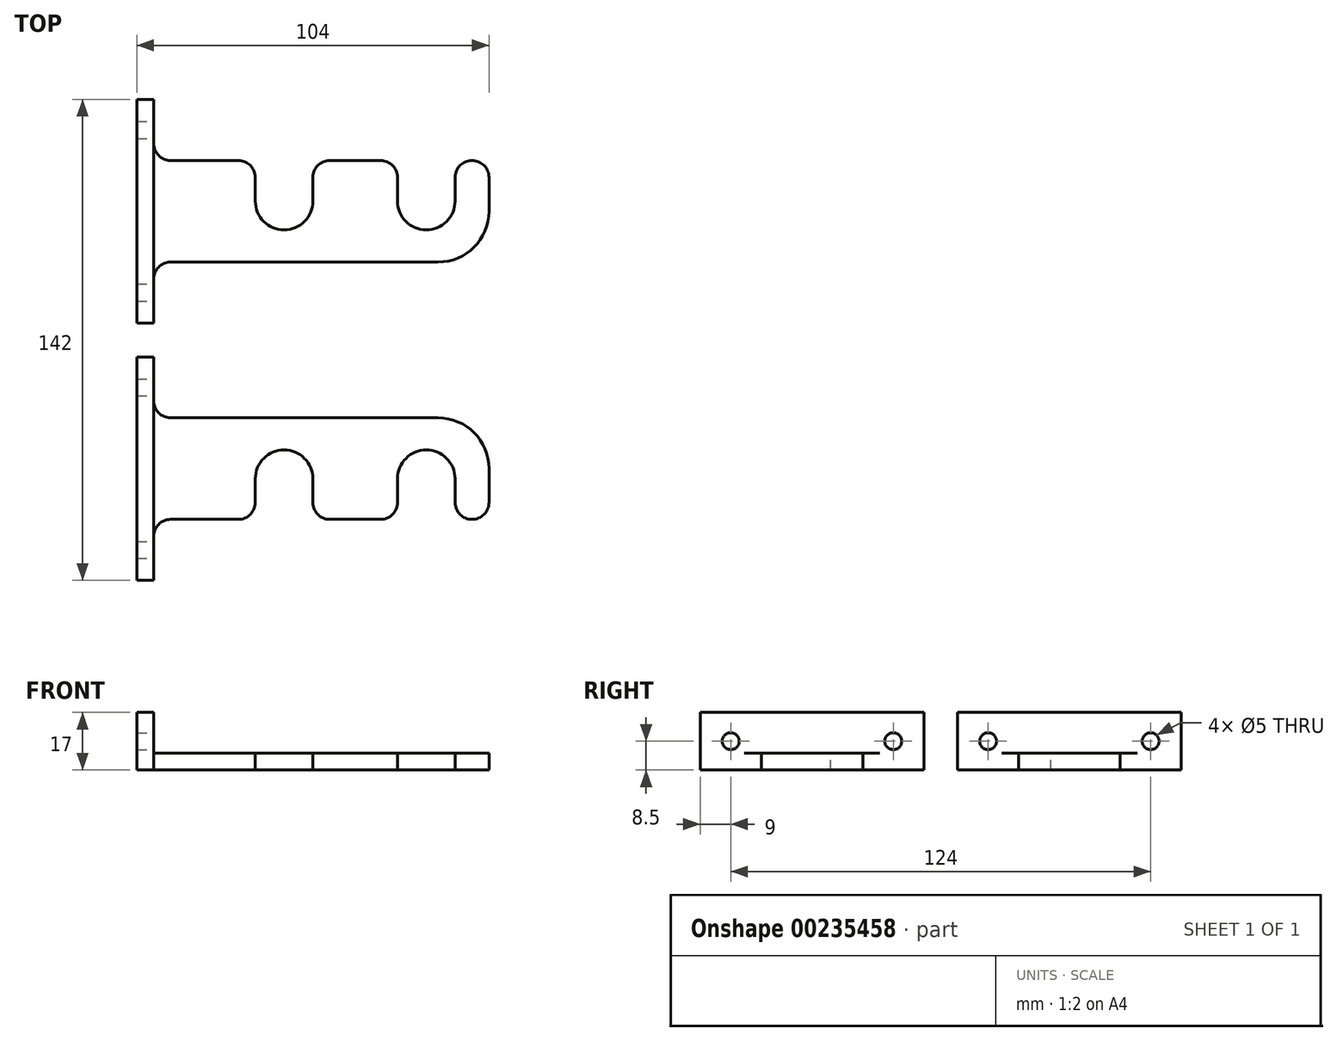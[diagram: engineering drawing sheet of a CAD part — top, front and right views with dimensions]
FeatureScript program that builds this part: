
annotation { "Feature Type Name" : "Feature", "Feature Type Description" : "" }
export const myFeature = defineFeature(function(context is Context, id is Id, definition is map)
    precondition{}
    {
        {
            var Q0;
            Q0=qCreatedBy(makeId("Front.planeOp"),FACE);
            var sketch = newSketch(context, id + "F0", { "sketchPlane" : qUnion([Q0])});
            skArc(sketch, "E0", {"start": v(28.28, 12.5) * mm, "mid": v(36.78, 4) * mm, "end": v(45.28, 12.5) * mm});
            skArc(sketch, "E1", {"start": v(70.28, 12.5) * mm, "mid": v(78.78, 4) * mm, "end": v(87.28, 12.5) * mm});
            skLineSegment(sketch, "E2", {"start": v(97.28, 12.5) * mm, "end": v(97.28, -5.5) * mm});
            skLineSegment(sketch, "E3", {"start": v(97.28, -5.5) * mm, "end": v(-1.72, -5.5) * mm});
            skLineSegment(sketch, "E4", {"start": v(-6.72, -5.5) * mm, "end": v(-6.72, 12.5) * mm});
            skLineSegment(sketch, "E5", {"start": v(28.28, 12.5) * mm, "end": v(28.28, 24.5) * mm});
            skLineSegment(sketch, "E6", {"start": v(28.28, 24.5) * mm, "end": v(-1.72, 24.5) * mm});
            skLineSegment(sketch, "E7", {"start": v(-6.72, 24.5) * mm, "end": v(-6.72, 12.5) * mm});
            skLineSegment(sketch, "E8.top", {"start": v(45.28, 24.5) * mm, "end": v(70.28, 24.5) * mm});
            skLineSegment(sketch, "E8.left", {"start": v(45.28, 12.5) * mm, "end": v(45.28, 24.5) * mm});
            skLineSegment(sketch, "E8.right", {"start": v(70.28, 12.5) * mm, "end": v(70.28, 24.5) * mm});
            skLineSegment(sketch, "E9.top", {"start": v(97.28, 24.5) * mm, "end": v(87.28, 24.5) * mm});
            skLineSegment(sketch, "E9.left", {"start": v(97.28, 12.5) * mm, "end": v(97.28, 24.5) * mm});
            skLineSegment(sketch, "E9.right", {"start": v(87.28, 12.5) * mm, "end": v(87.28, 24.5) * mm});
            skPoint(sketch, "E10.start.orphan", {"position": v(87.28, 12.5) * mm});
            skPoint(sketch, "E11.end.orphan", {"position": v(70.28, 12.5) * mm});
            skLineSegment(sketch, "E12.top", {"start": v(-6.72, -23.5) * mm, "end": v(-1.72, -23.5) * mm});
            skLineSegment(sketch, "E12.left", {"start": v(-6.72, -5.5) * mm, "end": v(-6.72, -23.5) * mm});
            skLineSegment(sketch, "E12.right", {"start": v(-1.72, -5.5) * mm, "end": v(-1.72, -23.5) * mm});
            skLineSegment(sketch, "E13.top", {"start": v(-6.72, 42.5) * mm, "end": v(-1.72, 42.5) * mm});
            skLineSegment(sketch, "E13.left", {"start": v(-6.72, 24.5) * mm, "end": v(-6.72, 42.5) * mm});
            skLineSegment(sketch, "E13.right", {"start": v(-1.72, 24.5) * mm, "end": v(-1.72, 42.5) * mm});
            skLineSegment(sketch, "E14", {"start": v(28.28, 12.5) * mm, "end": v(87.28, 12.5) * mm, "construction": true});
            skLineSegment(sketch, "E15", {"start": v(87.28, 12.5) * mm, "end": v(97.28, 12.5) * mm, "construction": true});
            skLineSegment(sketch, "E16", {"start": v(-1.72, 24.5) * mm, "end": v(-1.72, -5.5) * mm});
            skSolve(sketch);
        }
        {
            var Q0;
            Q0=makeQuery(id+"F0.imprint","IMPRINT",FACE,{"disambiguationData":[TD([[makeQuery(id+"F0.imprint","IMPRINT",EDGE,{"derivedFrom":sQuery(id+"F0.wireOp",EDGE,"E0")}),-1.0]])]});
            var Q1;
            Q1=makeQuery(id+"F0.imprint","IMPRINT",FACE,{"disambiguationData":[TD([[makeQuery(id+"F0.imprint","IMPRINT",EDGE,{"derivedFrom":sQuery(id+"F0.wireOp",EDGE,"E4")}),-1.0]])]});
            extrude(context, id + "F1", {"entities" : qUnion([Q0, Q1]), "depth" : 5 * mm});
        }
        {
            var Q0;
            {var subQ0=sQuery(id+"F0.wireOp",EDGE,"E13.left");var subQ1=sQuery(id+"F0.wireOp",EDGE,"E12.left");var subQ2=sQuery(id+"F0.wireOp",EDGE,"E7");var subQ3=sQuery(id+"F0.wireOp",EDGE,"E4");var subQ4=sQuery(id+"F0.wireOp",EDGE,"E13.top");var subQ5=sQuery(id+"F0.wireOp",EDGE,"E13.right");Q0=makeQuery(id+"F5.boolean.opBoolean","SPLIT",FACE,{"disambiguationData":[TD([makeQuery(id+"F1.opExtrude","SWEPT_FACE",FACE,{"disambiguationData":[OSD([subQ4])]})])],"derivedFrom":makeQuery(id+"F1.opExtrude","CAP_FACE",FACE,{"disambiguationData":[OSD([sQuery(id+"F0.wireOp",EDGE,"E0"),sQuery(id+"F0.wireOp",EDGE,"E1"),sQuery(id+"F0.wireOp",EDGE,"E2"),sQuery(id+"F0.wireOp",EDGE,"E3"),subQ3,sQuery(id+"F0.wireOp",EDGE,"E5"),sQuery(id+"F0.wireOp",EDGE,"E6"),subQ2,sQuery(id+"F0.wireOp",EDGE,"E8.top"),sQuery(id+"F0.wireOp",EDGE,"E8.left"),sQuery(id+"F0.wireOp",EDGE,"E8.right"),sQuery(id+"F0.wireOp",EDGE,"E9.top"),sQuery(id+"F0.wireOp",EDGE,"E9.left"),sQuery(id+"F0.wireOp",EDGE,"E9.right"),sQuery(id+"F0.wireOp",EDGE,"E12.top"),subQ1,sQuery(id+"F0.wireOp",EDGE,"E12.right"),subQ4,subQ0,subQ5])],"isStart":true})});}
            var sketch = newSketch(context, id + "F2", { "sketchPlane" : qUnion([Q0])});
            skLineSegment(sketch, "E17", {"start": v(1.72, 42.5) * mm, "end": v(1.72, -23.43) * mm});
            skPoint(sketch, "E17.endSnap0", {"position": v(1.72, 33.5) * mm});
            skSolve(sketch);
        }
        {
            var Q0;
            {var subQ4=makeQuery(id+"F1.opExtrude","CAP_EDGE",EDGE,{"disambiguationData":[OSD([sQuery(id+"F0.wireOp",EDGE,"E12.top")])],"isStart":true});Q0=makeQuery(id+"F2.imprint","IMPRINT",FACE,{"disambiguationData":[TD([[makeQuery(id+"F2.imprint","IMPRINT",EDGE,{"derivedFrom":subQ4}),-1.0]])]});}
            extrude(context, id + "F3", {"entities" : qUnion([Q0]), "operationType" : NewBodyOperationType.ADD, "depth" : 12 * mm});
        }
        {
            var Q0;
            Q0=makeQuery(id+"F1.opExtrude","SWEPT_FACE",FACE,{"disambiguationData":[OSD([sQuery(id+"F0.wireOp",EDGE,"E13.right")])]});
            var sketch = newSketch(context, id + "F4", { "sketchPlane" : qUnion([Q0])});
            skLineSegment(sketch, "E18.0.1", {"start": v(0, -5.5) * mm, "end": v(-5, -5.5) * mm});
            skLineSegment(sketch, "E18.0.2", {"start": v(-5, -5.5) * mm, "end": v(-5, -23.5) * mm});
            skLineSegment(sketch, "E18.0.3", {"start": v(-5, -23.5) * mm, "end": v(12, -23.5) * mm});
            skLineSegment(sketch, "E19", {"start": v(3.5, 42.5) * mm, "end": v(3.5, -23.5) * mm, "construction": true});
            skLineSegment(sketch, "E20", {"start": v(-5, 33.5) * mm, "end": v(12, 33.5) * mm, "construction": true});
            skLineSegment(sketch, "E21", {"start": v(-5, -14.5) * mm, "end": v(12, -14.5) * mm, "construction": true});
            skCircle(sketch, "E22", {"center": v(3.5, -14.5) * mm, "radius": 2.5 * mm});
            skCircle(sketch, "E23", {"center": v(3.5, 33.5) * mm, "radius": 2.5 * mm});
            skSolve(sketch);
        }
        {
            var Q0;
            Q0=makeQuery(id+"F4.imprint","IMPRINT",FACE,{"disambiguationData":[TD([[makeQuery(id+"F4.imprint","IMPRINT",EDGE,{"derivedFrom":sQuery(id+"F4.wireOp",EDGE,"E23")}),1.0]])]});
            var Q1;
            Q1=makeQuery(id+"F4.imprint","IMPRINT",FACE,{"disambiguationData":[TD([[makeQuery(id+"F4.imprint","IMPRINT",EDGE,{"derivedFrom":sQuery(id+"F4.wireOp",EDGE,"E22")}),1.0]])]});
            var Q2;
            Q2=sQuery(id+"F4.wireOp",EDGE,"E23");
            var Q3;
            Q3=sQuery(id+"F4.wireOp",EDGE,"E22");
            extrude(context, id + "F5", {"entities" : qUnion([Q0, Q1]), "operationType" : NewBodyOperationType.REMOVE, "surfaceEntities" : qUnion([Q2, Q3]), "endBound" : BoundingType.THROUGH_ALL, "oppositeDirection" : true, "depth" : 25 * mm});
        }
        {
            var Q0;
            Q0=makeQuery(id+"F1.opExtrude","SWEPT_EDGE",EDGE,{"disambiguationData":[OSD([sQuery(id+"F0.wireOp",EDGE,"E6"),sQuery(id+"F0.wireOp",EDGE,"E13.right")])]});
            var Q1;
            Q1=makeQuery(id+"F1.opExtrude","SWEPT_EDGE",EDGE,{"disambiguationData":[OSD([sQuery(id+"F0.wireOp",EDGE,"E3"),sQuery(id+"F0.wireOp",EDGE,"E12.right")])]});
            var Q2;
            Q2=makeQuery(id+"F1.opExtrude","SWEPT_EDGE",EDGE,{"disambiguationData":[OSD([sQuery(id+"F0.wireOp",EDGE,"E9.top"),sQuery(id+"F0.wireOp",EDGE,"E9.left")])]});
            var Q3;
            Q3=makeQuery(id+"F1.opExtrude","SWEPT_EDGE",EDGE,{"disambiguationData":[OSD([sQuery(id+"F0.wireOp",EDGE,"E5"),sQuery(id+"F0.wireOp",EDGE,"E6")])]});
            var Q4;
            Q4=makeQuery(id+"F1.opExtrude","SWEPT_EDGE",EDGE,{"disambiguationData":[OSD([sQuery(id+"F0.wireOp",EDGE,"E8.top"),sQuery(id+"F0.wireOp",EDGE,"E8.right")])]});
            var Q5;
            Q5=makeQuery(id+"F1.opExtrude","SWEPT_EDGE",EDGE,{"disambiguationData":[OSD([sQuery(id+"F0.wireOp",EDGE,"E9.top"),sQuery(id+"F0.wireOp",EDGE,"E9.right")])]});
            var Q6;
            Q6=makeQuery(id+"F1.opExtrude","SWEPT_EDGE",EDGE,{"disambiguationData":[OSD([sQuery(id+"F0.wireOp",EDGE,"E8.top"),sQuery(id+"F0.wireOp",EDGE,"E8.left")])]});
            var Q7;
            Q7=makeQuery(id+"F3.opExtrude","CAP_EDGE",EDGE,{"disambiguationData":[OSD([sQuery(id+"F2.wireOp",EDGE,"E17")])],"isStart":true});
            fillet(context, id + "F6", {"entities" : qUnion([Q0, Q1, Q2, Q3, Q4, Q5, Q6, Q7]), "radius" : 5 * mm, "tangentPropagation" : true, "allowEdgeOverflow" : false});
        }
        {
            var Q0;
            Q0=makeQuery(id+"F1.opExtrude","SWEPT_EDGE",EDGE,{"disambiguationData":[OSD([sQuery(id+"F0.wireOp",EDGE,"E2"),sQuery(id+"F0.wireOp",EDGE,"E3")])]});
            fillet(context, id + "F7", {"entities" : qUnion([Q0]), "radius" : 15 * mm, "tangentPropagation" : true, "allowEdgeOverflow" : false});
        }
        {
            var Q0;
            Q0=makeQuery(id+"F1.opExtrude","SWEPT_BODY",BODY,{"disambiguationData":[OSD([sQuery(id+"F0.wireOp",EDGE,"E0"),sQuery(id+"F0.wireOp",EDGE,"E1"),sQuery(id+"F0.wireOp",EDGE,"E2"),sQuery(id+"F0.wireOp",EDGE,"E3"),sQuery(id+"F0.wireOp",EDGE,"E4"),sQuery(id+"F0.wireOp",EDGE,"E5"),sQuery(id+"F0.wireOp",EDGE,"E6"),sQuery(id+"F0.wireOp",EDGE,"E7"),sQuery(id+"F0.wireOp",EDGE,"E8.top"),sQuery(id+"F0.wireOp",EDGE,"E8.left"),sQuery(id+"F0.wireOp",EDGE,"E8.right"),sQuery(id+"F0.wireOp",EDGE,"E9.top"),sQuery(id+"F0.wireOp",EDGE,"E9.left"),sQuery(id+"F0.wireOp",EDGE,"E9.right"),sQuery(id+"F0.wireOp",EDGE,"E12.top"),sQuery(id+"F0.wireOp",EDGE,"E12.left"),sQuery(id+"F0.wireOp",EDGE,"E12.right"),sQuery(id+"F0.wireOp",EDGE,"E13.top"),sQuery(id+"F0.wireOp",EDGE,"E13.left"),sQuery(id+"F0.wireOp",EDGE,"E13.right")])]});
            var Q1;
            Q1=makeQuery(id+"F1.opExtrude","CAP_EDGE",EDGE,{"disambiguationData":[OSD([sQuery(id+"F0.wireOp",EDGE,"E3")])],"isStart":false});
            transform(context, id + "F8", {"entities" : qUnion([Q0]), "transformType" : TransformType.ROTATION, "transformAxis" : qUnion([Q1]), "angle" : 90 * degree, "oppositeDirection" : true, "makeCopy" : false});
        }
        {
            var Q0;
            {var subQ0=sQuery(id+"F0.wireOp",EDGE,"E12.top");Q0=makeQuery(id+"F3.boolean.opBoolean","MERGE",FACE,{"derivedFrom":[makeQuery(id+"F1.opExtrude","SWEPT_FACE",FACE,{"disambiguationData":[OSD([subQ0])]}),makeQuery(id+"F3.opExtrude","SWEPT_FACE",FACE,{"disambiguationData":[OSD([subQ0])]})]});}
            cPlane(context, id + "F9", {"entities" : qUnion([Q0]), "cplaneType" : CPlaneType.OFFSET, "offset" : 5 * mm, "width" : 150 * mm, "height" : 150 * mm});
        }
        {
            var Q0;
            Q0=makeQuery(id+"F1.opExtrude","SWEPT_BODY",BODY,{"disambiguationData":[OSD([sQuery(id+"F0.wireOp",EDGE,"E0"),sQuery(id+"F0.wireOp",EDGE,"E1"),sQuery(id+"F0.wireOp",EDGE,"E2"),sQuery(id+"F0.wireOp",EDGE,"E3"),sQuery(id+"F0.wireOp",EDGE,"E4"),sQuery(id+"F0.wireOp",EDGE,"E5"),sQuery(id+"F0.wireOp",EDGE,"E6"),sQuery(id+"F0.wireOp",EDGE,"E7"),sQuery(id+"F0.wireOp",EDGE,"E8.top"),sQuery(id+"F0.wireOp",EDGE,"E8.left"),sQuery(id+"F0.wireOp",EDGE,"E8.right"),sQuery(id+"F0.wireOp",EDGE,"E9.top"),sQuery(id+"F0.wireOp",EDGE,"E9.left"),sQuery(id+"F0.wireOp",EDGE,"E9.right"),sQuery(id+"F0.wireOp",EDGE,"E12.top"),sQuery(id+"F0.wireOp",EDGE,"E12.left"),sQuery(id+"F0.wireOp",EDGE,"E12.right"),sQuery(id+"F0.wireOp",EDGE,"E13.top"),sQuery(id+"F0.wireOp",EDGE,"E13.left"),sQuery(id+"F0.wireOp",EDGE,"E13.right")])]});
            var Q1;
            Q1=qCreatedBy(id+"F9.planeOp",FACE);
            mirror(context, id + "F10", {"entities" : qUnion([Q0]), "mirrorPlane" : qUnion([Q1])});
        }
    });
